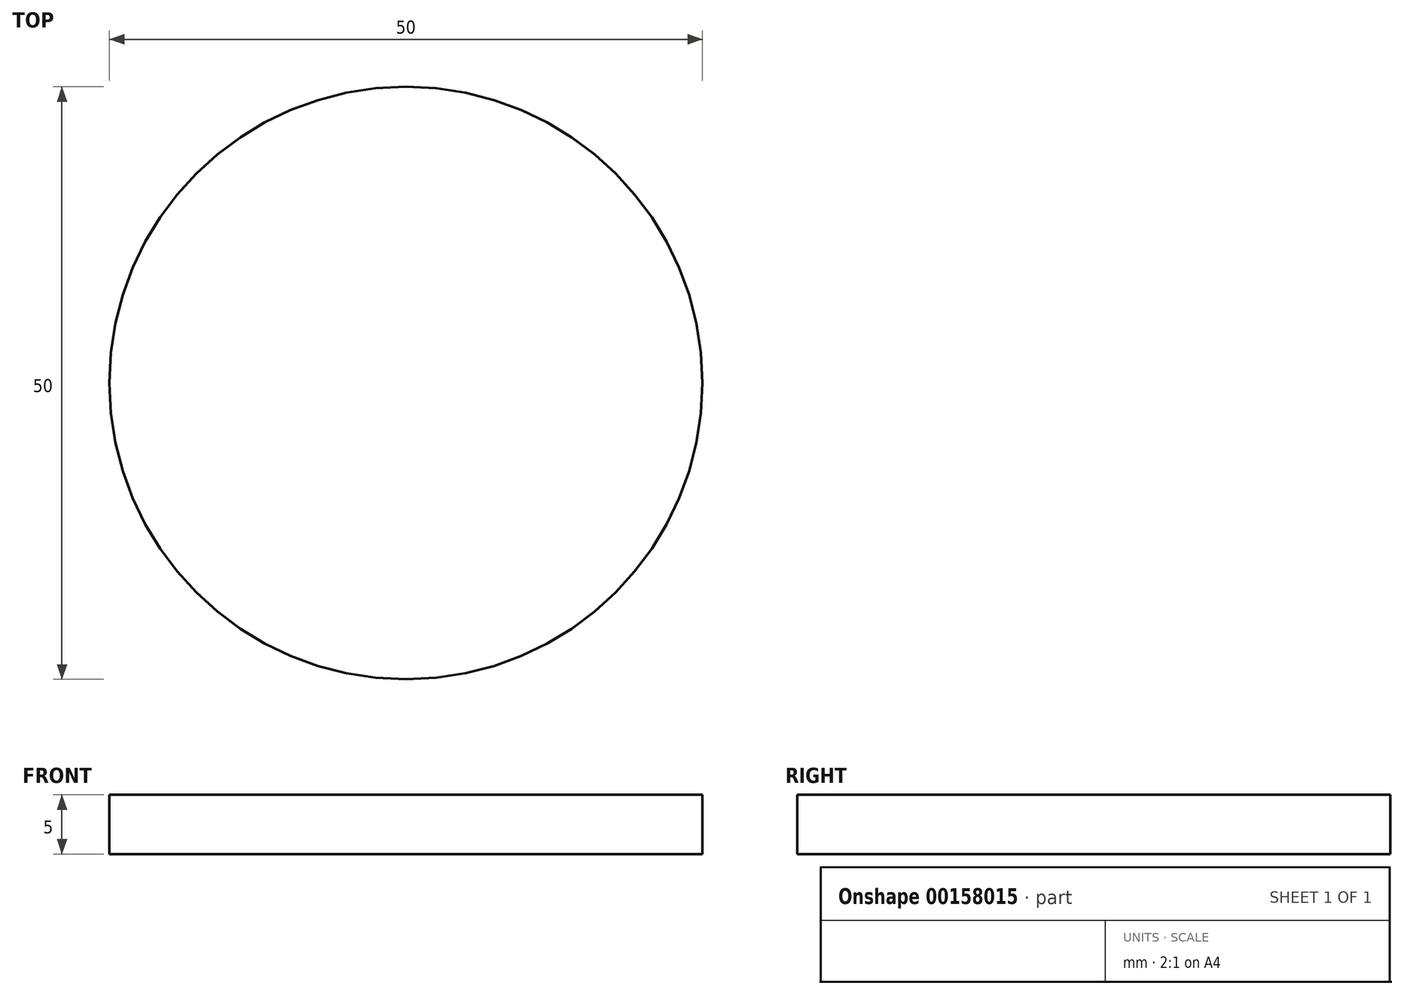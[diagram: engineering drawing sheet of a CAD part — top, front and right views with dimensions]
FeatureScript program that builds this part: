
annotation { "Feature Type Name" : "Feature", "Feature Type Description" : "" }
export const myFeature = defineFeature(function(context is Context, id is Id, definition is map)
    precondition{}
    {
        {
            var Q0;
            Q0=qCreatedBy(makeId("Top.planeOp"),FACE);
            var sketch = newSketch(context, id + "F0", { "sketchPlane" : qUnion([Q0])});
            skCircle(sketch, "E0", {"center": v(0, 0) * mm, "radius": 25 * mm});
            skCircle(sketch, "E1", {"center": v(0, 0) * mm, "radius": 15 * mm});
            skCircle(sketch, "E2", {"center": v(0, 0) * mm, "radius": 20 * mm});
            skSolve(sketch);
        }
        {
            var Q0;
            Q0=makeQuery(id+"F0.imprint","IMPRINT",FACE,{"disambiguationData":[TD([[makeQuery(id+"F0.imprint","IMPRINT",EDGE,{"derivedFrom":sQuery(id+"F0.wireOp",EDGE,"E1")}),-1.0]])]});
            var Q1;
            Q1=makeQuery(id+"F0.imprint","IMPRINT",FACE,{"disambiguationData":[TD([[makeQuery(id+"F0.imprint","IMPRINT",EDGE,{"derivedFrom":sQuery(id+"F0.wireOp",EDGE,"E1")}),1.0]])]});
            var Q2;
            Q2=makeQuery(id+"F0.imprint","IMPRINT",FACE,{"disambiguationData":[TD([[makeQuery(id+"F0.imprint","IMPRINT",EDGE,{"derivedFrom":sQuery(id+"F0.wireOp",EDGE,"E0")}),1.0]])]});
            extrude(context, id + "F1", {"entities" : qUnion([Q0, Q1, Q2]), "depth" : 5 * mm});
        }
    });
